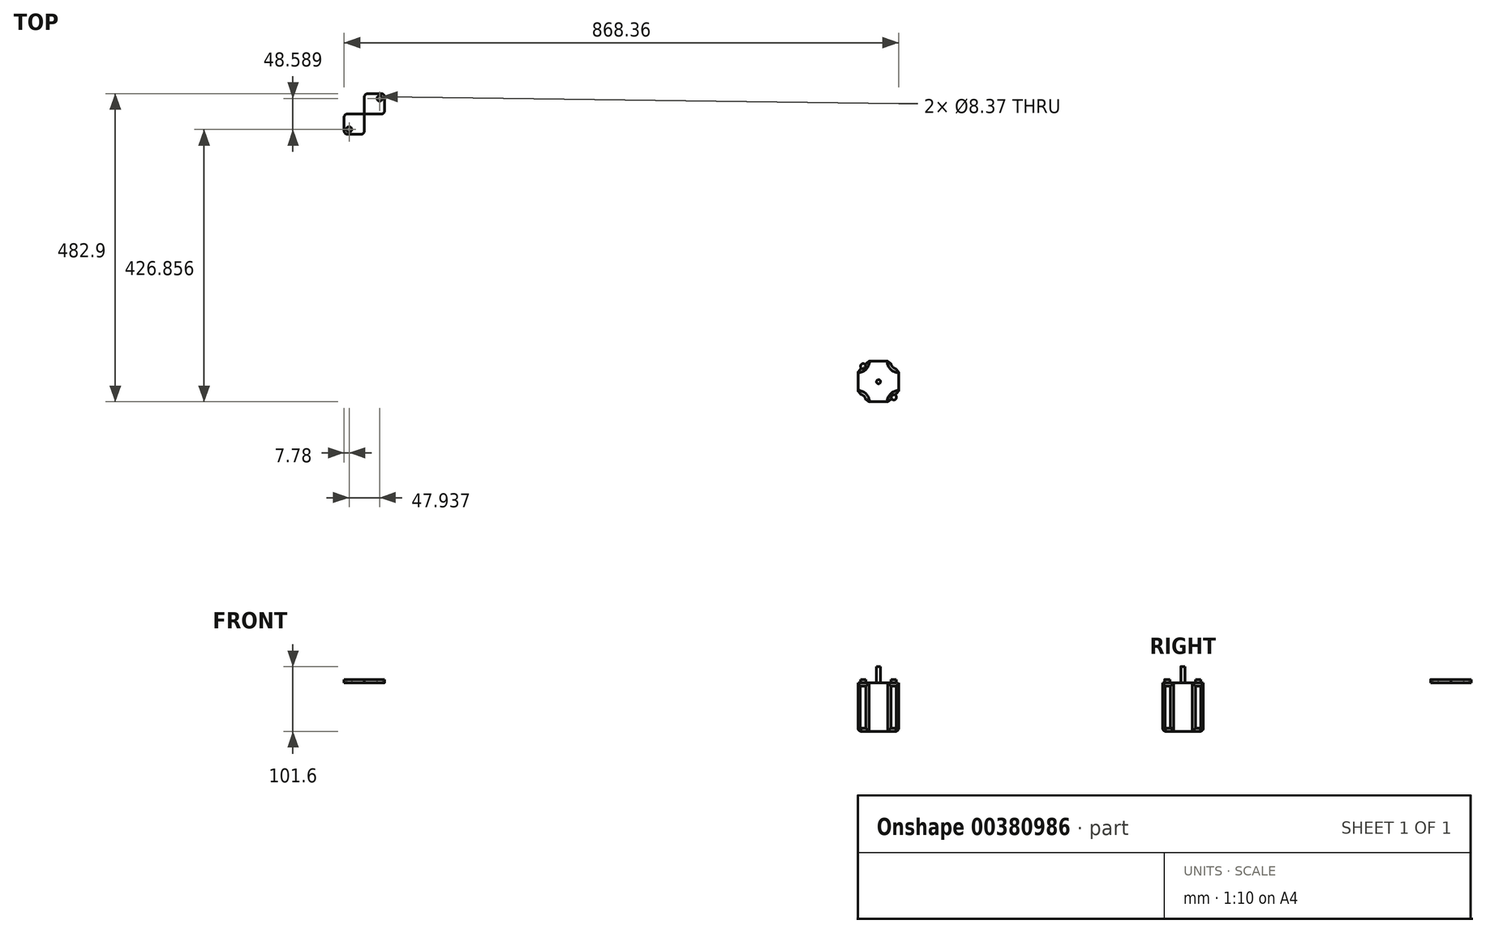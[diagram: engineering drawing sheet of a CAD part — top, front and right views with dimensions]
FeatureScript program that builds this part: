
annotation { "Feature Type Name" : "Feature", "Feature Type Description" : "" }
export const myFeature = defineFeature(function(context is Context, id is Id, definition is map)
    precondition{}
    {
        {
            var Q0;
            Q0=qCreatedBy(makeId("Top.planeOp"),FACE);
            var sketch = newSketch(context, id + "F0", { "sketchPlane" : qUnion([Q0])});
            skLineSegment(sketch, "E0.bottom", {"start": v(-29.8, -20.16) * mm, "end": v(33.7, -20.16) * mm});
            skLineSegment(sketch, "E0.top", {"start": v(-29.8, 43.34) * mm, "end": v(33.7, 43.34) * mm});
            skLineSegment(sketch, "E0.left", {"start": v(-29.8, -20.16) * mm, "end": v(-29.8, 43.34) * mm});
            skLineSegment(sketch, "E0.right", {"start": v(33.7, -20.16) * mm, "end": v(33.7, 43.34) * mm});
            skCircle(sketch, "E1", {"center": v(-22.02, -12.7) * mm, "radius": 4.18 * mm});
            skLineSegment(sketch, "E2", {"start": v(1.95, -20.16) * mm, "end": v(1.95, 43.34) * mm});
            skLineSegment(sketch, "E3", {"start": v(-29.8, 11.6) * mm, "end": v(33.7, 11.6) * mm});
            skCircle(sketch, "E4.MirrorC", {"center": v(-22.02, 35.88) * mm, "radius": 4.18 * mm});
            skCircle(sketch, "E5.MirrorC", {"center": v(25.92, 35.88) * mm, "radius": 4.18 * mm});
            skCircle(sketch, "E6.MirrorC", {"center": v(25.92, -12.7) * mm, "radius": 4.18 * mm});
            skSolve(sketch);
        }
        {
            var Q0;
            Q0=makeQuery(id+"F0.imprint","IMPRINT",FACE,{"disambiguationData":[TD([[makeQuery(id+"F0.imprint","IMPRINT",EDGE,{"derivedFrom":sQuery(id+"F0.wireOp",EDGE,"E6.MirrorC")}),1.0]])]});
            var Q1;
            Q1=makeQuery(id+"F0.imprint","IMPRINT",FACE,{"disambiguationData":[TD([[makeQuery(id+"F0.imprint","IMPRINT",EDGE,{"derivedFrom":sQuery(id+"F0.wireOp",EDGE,"E1")}),-1.0]])]});
            var Q2;
            Q2=makeQuery(id+"F0.imprint","IMPRINT",FACE,{"disambiguationData":[TD([[makeQuery(id+"F0.imprint","IMPRINT",EDGE,{"derivedFrom":sQuery(id+"F0.wireOp",EDGE,"E4.MirrorC")}),1.0]])]});
            var Q3;
            Q3=makeQuery(id+"F0.imprint","IMPRINT",FACE,{"disambiguationData":[TD([[makeQuery(id+"F0.imprint","IMPRINT",EDGE,{"derivedFrom":sQuery(id+"F0.wireOp",EDGE,"E5.MirrorC")}),-1.0]])]});
            extrude(context, id + "F1", {"entities" : qUnion([Q0, Q1, Q2, Q3]), "depth" : 5.08 * mm});
        }
        {
            var Q0;
            Q0=makeQuery(id+"F1.opExtrude","SWEPT_BODY",BODY,{"disambiguationData":[OSD([sQuery(id+"F0.wireOp",EDGE,"E0.bottom"),sQuery(id+"F0.wireOp",EDGE,"E0.top"),sQuery(id+"F0.wireOp",EDGE,"E0.left"),sQuery(id+"F0.wireOp",EDGE,"E0.right"),sQuery(id+"F0.wireOp",EDGE,"E1"),sQuery(id+"F0.wireOp",EDGE,"E4.MirrorC"),sQuery(id+"F0.wireOp",EDGE,"E5.MirrorC"),sQuery(id+"F0.wireOp",EDGE,"E6.MirrorC")])]});
            transform(context, id + "F2", {"entities" : qUnion([Q0]), "transformType" : TransformType.TRANSLATION_3D, "dx" : 0 * mm, "dy" : 71.57 * mm, "dz" : 0 * mm, "makeCopy" : false});
        }
        {
            var Q0;
            Q0=makeQuery(id+"F1.opExtrude","SWEPT_EDGE",EDGE,{"disambiguationData":[OSD([sQuery(id+"F0.wireOp",EDGE,"E0.top"),sQuery(id+"F0.wireOp",EDGE,"E0.right")])]});
            var Q1;
            Q1=makeQuery(id+"F1.opExtrude","SWEPT_EDGE",EDGE,{"disambiguationData":[OSD([sQuery(id+"F0.wireOp",EDGE,"E0.bottom"),sQuery(id+"F0.wireOp",EDGE,"E0.right")])]});
            var Q2;
            Q2=makeQuery(id+"F1.opExtrude","SWEPT_EDGE",EDGE,{"disambiguationData":[OSD([sQuery(id+"F0.wireOp",EDGE,"E0.bottom"),sQuery(id+"F0.wireOp",EDGE,"E0.left")])]});
            var Q3;
            Q3=makeQuery(id+"F1.opExtrude","SWEPT_EDGE",EDGE,{"disambiguationData":[OSD([sQuery(id+"F0.wireOp",EDGE,"E0.top"),sQuery(id+"F0.wireOp",EDGE,"E0.left")])]});
            fillet(context, id + "F3", {"entities" : qUnion([Q0, Q1, Q2, Q3]), "radius" : 5.08 * mm, "tangentPropagation" : true, "allowEdgeOverflow" : false});
        }
        {
            var Q0;
            Q0=makeQuery(id+"F1.opExtrude","SWEPT_BODY",BODY,{"disambiguationData":[OSD([sQuery(id+"F0.wireOp",EDGE,"E0.bottom"),sQuery(id+"F0.wireOp",EDGE,"E0.top"),sQuery(id+"F0.wireOp",EDGE,"E0.left"),sQuery(id+"F0.wireOp",EDGE,"E0.right"),sQuery(id+"F0.wireOp",EDGE,"E1"),sQuery(id+"F0.wireOp",EDGE,"E4.MirrorC"),sQuery(id+"F0.wireOp",EDGE,"E5.MirrorC"),sQuery(id+"F0.wireOp",EDGE,"E6.MirrorC")])]});
            var Q1;
            Q1=makeQuery(id+"F1.opExtrude","SWEPT_FACE",FACE,{"disambiguationData":[OSD([sQuery(id+"F0.wireOp",EDGE,"E0.right")])]});
            mirror(context, id + "F4", {"entities" : qUnion([Q0]), "mirrorPlane" : qUnion([Q1])});
        }
        {
            var Q0;
            Q0=makeQuery(id+"F4.opPattern","COPY",BODY,{"derivedFrom":makeQuery(id+"F1.opExtrude","SWEPT_BODY",BODY,{"disambiguationData":[OSD([sQuery(id+"F0.wireOp",EDGE,"E0.bottom"),sQuery(id+"F0.wireOp",EDGE,"E0.top"),sQuery(id+"F0.wireOp",EDGE,"E0.left"),sQuery(id+"F0.wireOp",EDGE,"E0.right"),sQuery(id+"F0.wireOp",EDGE,"E1"),sQuery(id+"F0.wireOp",EDGE,"E4.MirrorC"),sQuery(id+"F0.wireOp",EDGE,"E5.MirrorC"),sQuery(id+"F0.wireOp",EDGE,"E6.MirrorC")])]}),"instanceName":"1"});
            deleteBodies(context, id + "F5", {"entities" : qUnion([Q0])});
        }
        {
            var Q0;
            Q0=qCreatedBy(makeId("Top.planeOp"),FACE);
            var sketch = newSketch(context, id + "F6", { "sketchPlane" : qUnion([Q0])});
            skLineSegment(sketch, "E7.bottom", {"start": v(43.89, -20.18) * mm, "end": v(107.39, -20.18) * mm});
            skLineSegment(sketch, "E7.top", {"start": v(43.89, 43.32) * mm, "end": v(107.39, 43.32) * mm});
            skLineSegment(sketch, "E7.left", {"start": v(43.89, -20.18) * mm, "end": v(43.89, 43.32) * mm});
            skLineSegment(sketch, "E7.right", {"start": v(107.39, -20.18) * mm, "end": v(107.39, 43.32) * mm});
            skLineSegment(sketch, "E8", {"start": v(75.64, -20.18) * mm, "end": v(75.64, 43.32) * mm});
            skLineSegment(sketch, "E9", {"start": v(43.89, 11.57) * mm, "end": v(107.39, 11.57) * mm});
            skCircle(sketch, "E10", {"center": v(43.89, -20.18) * mm, "radius": 12.7 * mm});
            skCircle(sketch, "E11", {"center": v(107.39, -20.18) * mm, "radius": 12.7 * mm});
            skCircle(sketch, "E12", {"center": v(107.39, 43.32) * mm, "radius": 12.7 * mm});
            skCircle(sketch, "E13", {"center": v(43.89, 43.32) * mm, "radius": 12.7 * mm});
            skSolve(sketch);
        }
        {
            var Q0;
            {var subQ3=sQuery(id+"F6.wireOp",EDGE,"E8");var subQ7=sQuery(id+"F6.wireOp",EDGE,"E7.bottom");var subQ9=makeQuery(id+"F6.imprint","INTERSECT",VERTEX,{"derivedFrom":[subQ7,subQ3]});Q0=makeQuery(id+"F6.imprint","IMPRINT",FACE,{"disambiguationData":[TD([[makeQuery(id+"F6.imprint","IMPRINT",EDGE,{"disambiguationData":[TD([[subQ9,1.0]])],"derivedFrom":subQ7}),1.0]])]});}
            var Q1;
            {var subQ3=sQuery(id+"F6.wireOp",EDGE,"E8");var subQ5=sQuery(id+"F6.wireOp",EDGE,"E7.bottom");var subQ6=makeQuery(id+"F6.imprint","INTERSECT",VERTEX,{"derivedFrom":[subQ5,subQ3]});Q1=makeQuery(id+"F6.imprint","IMPRINT",FACE,{"disambiguationData":[TD([[makeQuery(id+"F6.imprint","IMPRINT",EDGE,{"disambiguationData":[TD([[subQ6,-1.0]])],"derivedFrom":subQ5}),1.0]])]});}
            var Q2;
            {var subQ3=sQuery(id+"F6.wireOp",EDGE,"E8");var subQ5=sQuery(id+"F6.wireOp",EDGE,"E7.top");var subQ6=makeQuery(id+"F6.imprint","INTERSECT",VERTEX,{"derivedFrom":[subQ5,subQ3]});Q2=makeQuery(id+"F6.imprint","IMPRINT",FACE,{"disambiguationData":[TD([[makeQuery(id+"F6.imprint","IMPRINT",EDGE,{"disambiguationData":[TD([[subQ6,1.0]])],"derivedFrom":subQ5}),-1.0]])]});}
            var Q3;
            {var subQ0=sQuery(id+"F6.wireOp",EDGE,"E8");var subQ1=sQuery(id+"F6.wireOp",EDGE,"E7.top");var subQ2=makeQuery(id+"F6.imprint","INTERSECT",VERTEX,{"derivedFrom":[subQ1,subQ0]});Q3=makeQuery(id+"F6.imprint","IMPRINT",FACE,{"disambiguationData":[TD([[makeQuery(id+"F6.imprint","IMPRINT",EDGE,{"disambiguationData":[TD([[subQ2,-1.0]])],"derivedFrom":subQ1}),-1.0]])]});}
            extrude(context, id + "F7", {"entities" : qUnion([Q0, Q1, Q2, Q3]), "oppositeDirection" : true, "depth" : 76.2 * mm});
        }
        {
            var Q0;
            Q0=qCreatedBy(makeId("Top.planeOp"),FACE);
            var sketch = newSketch(context, id + "F8", { "sketchPlane" : qUnion([Q0])});
            skCircle(sketch, "E14", {"center": v(15.6, -39.45) * mm, "radius": 3.18 * mm});
            skSolve(sketch);
        }
        {
            var Q0;
            Q0 = qSketchRegion(id + "F8", true);
            extrude(context, id + "F9", {"entities" : qUnion([Q0]), "depth" : 25.4 * mm});
        }
        {
            var Q0;
            Q0=makeQuery(id+"F9.opExtrude","SWEPT_BODY",BODY,{"disambiguationData":[OSD([sQuery(id+"F8.wireOp",EDGE,"E14")])]});
            transform(context, id + "F10", {"entities" : qUnion([Q0]), "transformType" : TransformType.TRANSLATION_3D, "dx" : 60.36 * mm, "dy" : 50.76 * mm, "dz" : 0 * mm, "makeCopy" : false});
        }
        {
            var Q0;
            Q0=makeQuery(id+"F1.opExtrude","SWEPT_BODY",BODY,{"disambiguationData":[OSD([sQuery(id+"F0.wireOp",EDGE,"E0.bottom"),sQuery(id+"F0.wireOp",EDGE,"E0.top"),sQuery(id+"F0.wireOp",EDGE,"E0.left"),sQuery(id+"F0.wireOp",EDGE,"E0.right"),sQuery(id+"F0.wireOp",EDGE,"E1"),sQuery(id+"F0.wireOp",EDGE,"E4.MirrorC"),sQuery(id+"F0.wireOp",EDGE,"E5.MirrorC"),sQuery(id+"F0.wireOp",EDGE,"E6.MirrorC")])]});
            transform(context, id + "F11", {"entities" : qUnion([Q0]), "transformType" : TransformType.TRANSLATION_3D, "dx" : 73.92 * mm, "dy" : -71.94 * mm, "dz" : 0 * mm, "makeCopy" : false});
        }
        {
            var Q0;
            Q0=makeQuery(id+"F7.opExtrude","CAP_EDGE",EDGE,{"disambiguationData":[OSD([sQuery(id+"F6.wireOp",EDGE,"E7.left")])],"isStart":false});
            var Q1;
            Q1=makeQuery(id+"F7.opExtrude","CAP_EDGE",EDGE,{"disambiguationData":[OSD([sQuery(id+"F6.wireOp",EDGE,"E7.top")])],"isStart":false});
            var Q2;
            Q2=makeQuery(id+"F7.opExtrude","CAP_EDGE",EDGE,{"disambiguationData":[OSD([sQuery(id+"F6.wireOp",EDGE,"E7.right")])],"isStart":false});
            var Q3;
            Q3=makeQuery(id+"F7.opExtrude","CAP_EDGE",EDGE,{"disambiguationData":[OSD([sQuery(id+"F6.wireOp",EDGE,"E7.bottom")])],"isStart":false});
            fillet(context, id + "F12", {"entities" : qUnion([Q0, Q1, Q2, Q3]), "radius" : 5.08 * mm, "tangentPropagation" : true, "allowEdgeOverflow" : false});
        }
        {
            var Q0;
            Q0=makeQuery(id+"F7.opExtrude","SWEPT_FACE",FACE,{"disambiguationData":[OSD([sQuery(id+"F6.wireOp",EDGE,"E12")])]});
            var Q1;
            Q1=makeQuery(id+"F7.opExtrude","SWEPT_FACE",FACE,{"disambiguationData":[OSD([sQuery(id+"F6.wireOp",EDGE,"E13")])]});
            var Q2;
            Q2=makeQuery(id+"F7.opExtrude","SWEPT_FACE",FACE,{"disambiguationData":[OSD([sQuery(id+"F6.wireOp",EDGE,"E10")])]});
            var Q3;
            Q3=makeQuery(id+"F7.opExtrude","SWEPT_FACE",FACE,{"disambiguationData":[OSD([sQuery(id+"F6.wireOp",EDGE,"E11")])]});
            chamfer(context, id + "F13", {"entities" : qUnion([Q0, Q1, Q2, Q3]), "width" : 5.08 * mm, "tangentPropagation" : true});
        }
        {
            var Q0;
            Q0=makeQuery(id+"F7.opExtrude","SWEPT_BODY",BODY,{"disambiguationData":[OSD([sQuery(id+"F6.wireOp",EDGE,"E7.bottom"),sQuery(id+"F6.wireOp",EDGE,"E7.top"),sQuery(id+"F6.wireOp",EDGE,"E7.left"),sQuery(id+"F6.wireOp",EDGE,"E7.right"),sQuery(id+"F6.wireOp",EDGE,"E10"),sQuery(id+"F6.wireOp",EDGE,"E11"),sQuery(id+"F6.wireOp",EDGE,"E12"),sQuery(id+"F6.wireOp",EDGE,"E13")])]});
            var Q1;
            Q1=makeQuery(id+"F1.opExtrude","SWEPT_BODY",BODY,{"disambiguationData":[OSD([sQuery(id+"F0.wireOp",EDGE,"E0.bottom"),sQuery(id+"F0.wireOp",EDGE,"E0.top"),sQuery(id+"F0.wireOp",EDGE,"E0.left"),sQuery(id+"F0.wireOp",EDGE,"E0.right"),sQuery(id+"F0.wireOp",EDGE,"E1"),sQuery(id+"F0.wireOp",EDGE,"E4.MirrorC"),sQuery(id+"F0.wireOp",EDGE,"E5.MirrorC"),sQuery(id+"F0.wireOp",EDGE,"E6.MirrorC")])]});
            var Q2;
            Q2=makeQuery(id+"F9.opExtrude","SWEPT_BODY",BODY,{"disambiguationData":[OSD([sQuery(id+"F8.wireOp",EDGE,"E14")])]});
            transform(context, id + "F14", {"entities" : qUnion([Q0, Q1, Q2]), "transformType" : TransformType.TRANSLATION_3D, "dx" : 266.62 * mm, "dy" : 0 * mm, "dz" : 0 * mm, "makeCopy" : false});
        }
        {
            var Q0;
            Q0=makeQuery(id+"F1.opExtrude","SWEPT_BODY",BODY,{"disambiguationData":[OSD([sQuery(id+"F0.wireOp",EDGE,"E0.bottom"),sQuery(id+"F0.wireOp",EDGE,"E0.top"),sQuery(id+"F0.wireOp",EDGE,"E0.left"),sQuery(id+"F0.wireOp",EDGE,"E0.right"),sQuery(id+"F0.wireOp",EDGE,"E1"),sQuery(id+"F0.wireOp",EDGE,"E4.MirrorC"),sQuery(id+"F0.wireOp",EDGE,"E5.MirrorC"),sQuery(id+"F0.wireOp",EDGE,"E6.MirrorC")])]});
            var Q1;
            Q1=makeQuery(id+"F7.opExtrude","SWEPT_BODY",BODY,{"disambiguationData":[OSD([sQuery(id+"F6.wireOp",EDGE,"E7.bottom"),sQuery(id+"F6.wireOp",EDGE,"E7.top"),sQuery(id+"F6.wireOp",EDGE,"E7.left"),sQuery(id+"F6.wireOp",EDGE,"E7.right"),sQuery(id+"F6.wireOp",EDGE,"E10"),sQuery(id+"F6.wireOp",EDGE,"E11"),sQuery(id+"F6.wireOp",EDGE,"E12"),sQuery(id+"F6.wireOp",EDGE,"E13")])]});
            var Q2;
            Q2=makeQuery(id+"F9.opExtrude","SWEPT_BODY",BODY,{"disambiguationData":[OSD([sQuery(id+"F8.wireOp",EDGE,"E14")])]});
            transform(context, id + "F15", {"entities" : qUnion([Q0, Q1, Q2]), "transformType" : TransformType.TRANSLATION_3D, "dx" : 464.56 * mm, "dy" : -419.38 * mm, "dz" : 0 * mm, "makeCopy" : false});
        }
    });
